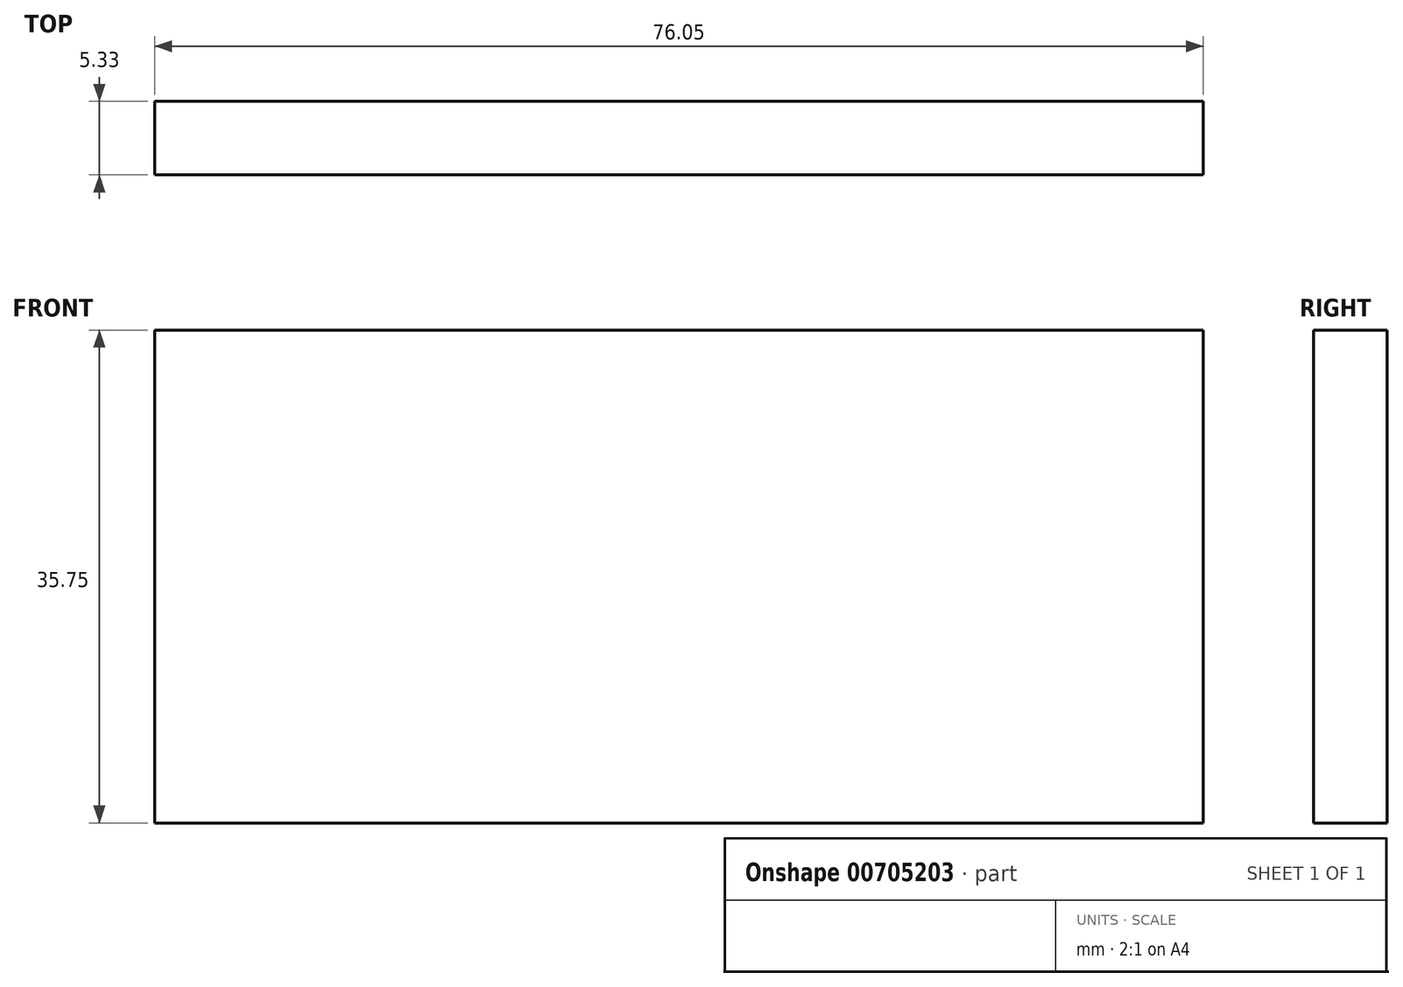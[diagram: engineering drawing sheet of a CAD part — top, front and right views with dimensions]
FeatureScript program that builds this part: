
annotation { "Feature Type Name" : "Feature", "Feature Type Description" : "" }
export const myFeature = defineFeature(function(context is Context, id is Id, definition is map)
    precondition{}
    {
        {
            var Q0;
            Q0=qCreatedBy(makeId("Front.planeOp"),FACE);
            var sketch = newSketch(context, id + "F0", { "sketchPlane" : qUnion([Q0])});
            skLineSegment(sketch, "E0.bottom", {"start": v(0, 0) * mm, "end": v(76.05, 0) * mm});
            skLineSegment(sketch, "E0.top", {"start": v(0, 35.75) * mm, "end": v(76.05, 35.75) * mm});
            skLineSegment(sketch, "E0.left", {"start": v(0, 0) * mm, "end": v(0, 35.75) * mm});
            skLineSegment(sketch, "E0.right", {"start": v(76.05, 0) * mm, "end": v(76.05, 35.75) * mm});
            skSolve(sketch);
        }
        {
            var Q0;
            Q0 = qSketchRegion(id + "F0", true);
            extrude(context, id + "F1", {"entities" : qUnion([Q0]), "depth" : 5.33 * mm, "offsetDistance" : 25.4 * mm});
        }
    });
